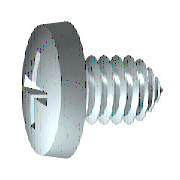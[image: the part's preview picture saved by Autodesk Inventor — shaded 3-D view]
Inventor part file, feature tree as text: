
AUTODESK INVENTOR PART (.ipt)
format: ipt  version: 2017 (Build 210142000, 142)  size: 248,320 bytes
history: native  units: mm (DEFAULTED — no unit token found)
features: other x2, plane x2, extrude x1
ambient origin geometry x8: Origin, YZ Plane, XZ Plane, XY Plane, X Axis, Y Axis, Z Axis, Center Point
bodies: Solid1 (feature_tree)
feature tree (5):
  other  "Corps"
  plane  "Work Plane1"
  extrude  "Rainure"  Depth=3.5mm
  other  "Coupe"
  plane  "Work Plane3"
